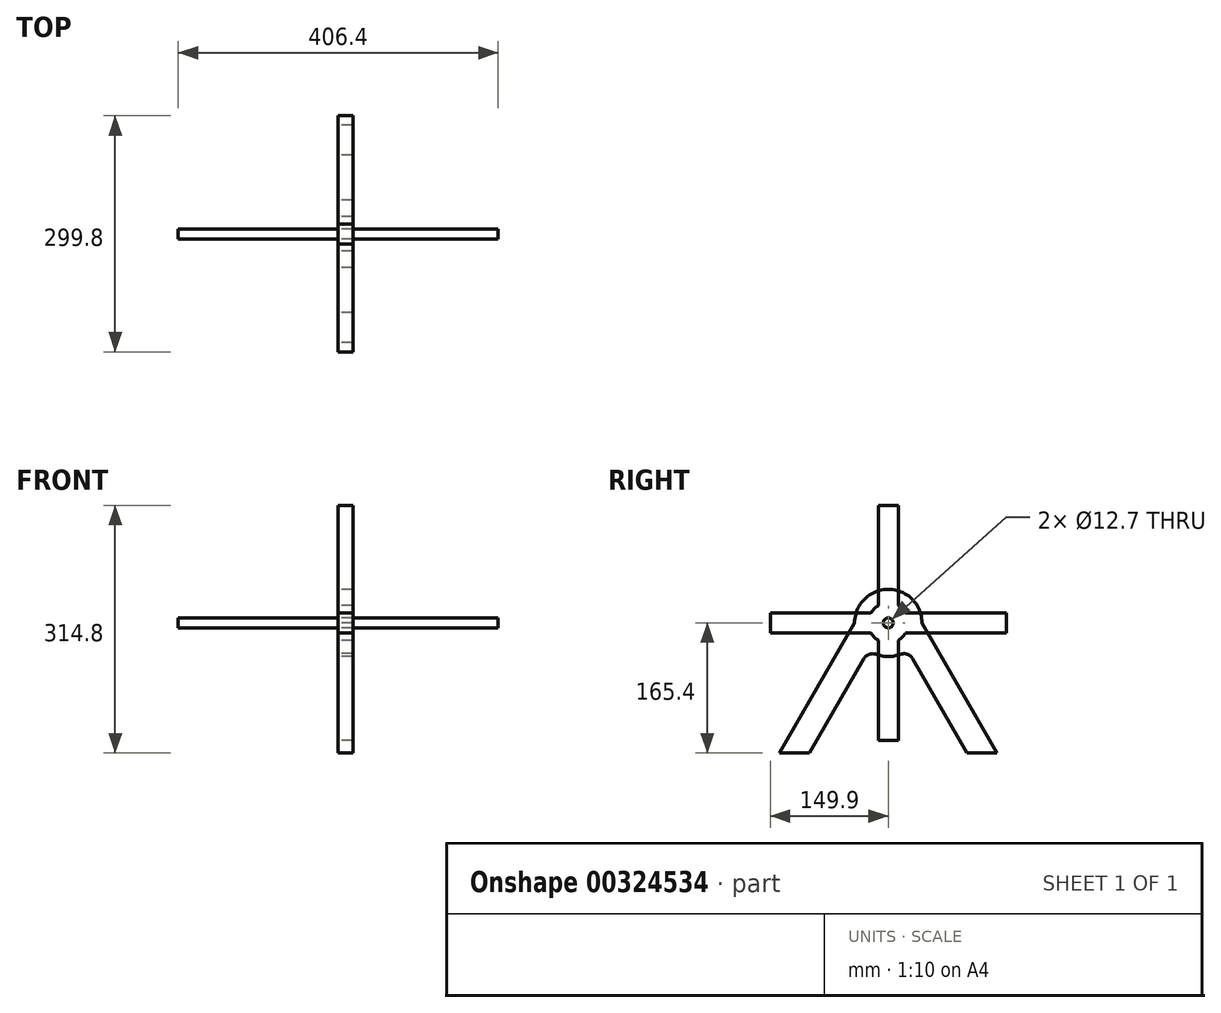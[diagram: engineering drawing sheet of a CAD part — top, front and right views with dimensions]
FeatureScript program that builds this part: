
annotation { "Feature Type Name" : "Feature", "Feature Type Description" : "" }
export const myFeature = defineFeature(function(context is Context, id is Id, definition is map)
    precondition{}
    {
        {
            var Q0;
            Q0=qCreatedBy(makeId("Right.planeOp"),FACE);
            var sketch = newSketch(context, id + "F0", { "sketchPlane" : qUnion([Q0])});
            skCircle(sketch, "E0", {"center": v(0, 0) * mm, "radius": 152.4 * mm});
            skSolve(sketch);
        }
        {
            var Q0;
            Q0=qCreatedBy(makeId("Right.planeOp"),FACE);
            var sketch = newSketch(context, id + "F1", { "sketchPlane" : qUnion([Q0])});
            skArc(sketch, "E1", {"start": v(-12.7, 22) * mm, "mid": v(-17.96, 17.96) * mm, "end": v(-22, 12.7) * mm});
            skCircle(sketch, "E2", {"center": v(0, 0) * mm, "radius": 6.35 * mm});
            skLineSegment(sketch, "E3.bottom", {"start": v(149.9, -12.7) * mm, "end": v(22, -12.7) * mm});
            skLineSegment(sketch, "E3.top", {"start": v(149.9, 12.7) * mm, "end": v(22, 12.7) * mm});
            skLineSegment(sketch, "E3.left", {"start": v(149.9, -12.7) * mm, "end": v(149.9, 12.7) * mm});
            skLineSegment(sketch, "E3.right", {"start": v(-149.9, -12.7) * mm, "end": v(-149.9, 12.7) * mm});
            skLineSegment(sketch, "E4.bottom", {"start": v(12.7, -149.4) * mm, "end": v(-12.7, -149.4) * mm});
            skLineSegment(sketch, "E4.top", {"start": v(12.7, 149.4) * mm, "end": v(-12.7, 149.4) * mm});
            skLineSegment(sketch, "E4.left", {"start": v(12.7, -149.4) * mm, "end": v(12.7, -22) * mm});
            skLineSegment(sketch, "E4.right", {"start": v(-12.7, -149.4) * mm, "end": v(-12.7, -12.7) * mm});
            skLineSegment(sketch, "E5.trimOffspring", {"start": v(-22, 12.7) * mm, "end": v(-149.9, 12.7) * mm});
            skLineSegment(sketch, "E6.trimOffspring", {"start": v(12.7, 22) * mm, "end": v(12.7, 149.4) * mm});
            skLineSegment(sketch, "E7.trimOffspring", {"start": v(-22, -12.7) * mm, "end": v(-149.9, -12.7) * mm});
            skLineSegment(sketch, "E8.trimOffspring", {"start": v(-12.7, 22) * mm, "end": v(-12.7, 149.4) * mm});
            skArc(sketch, "E9.trimOffspring", {"start": v(22, 12.7) * mm, "mid": v(17.96, 17.96) * mm, "end": v(12.7, 22) * mm});
            skArc(sketch, "E10.trimOffspring", {"start": v(12.7, -22) * mm, "mid": v(17.96, -17.96) * mm, "end": v(22, -12.7) * mm});
            skArc(sketch, "E11.trimOffspring", {"start": v(-22, -12.7) * mm, "mid": v(-17.96, -17.96) * mm, "end": v(-12.7, -22) * mm});
            skSolve(sketch);
        }
        {
            var Q0;
            Q0 = qSketchRegion(id + "F1", true);
            extrude(context, id + "F2", {"entities" : qUnion([Q0]), "depth" : 19.05 * mm});
        }
        {
            var Q0;
            Q0=makeQuery(id+"F0.imprint","IMPRINT",FACE,{"disambiguationData":[TD([[makeQuery(id+"F0.imprint","IMPRINT",EDGE,{"derivedFrom":sQuery(id+"F0.wireOp",EDGE,"E0")}),1.0]])]});
            var sketch = newSketch(context, id + "F3", { "sketchPlane" : qUnion([Q0])});
            skCircle(sketch, "E12.0", {"center": v(0, 0) * mm, "radius": 6.35 * mm});
            skSolve(sketch);
        }
        {
            var Q0;
            Q0 = qSketchRegion(id + "F3", true);
            extrude(context, id + "F4", {"entities" : qUnion([Q0]), "endBound" : BoundingType.SYMMETRIC, "depth" : 406.4 * mm});
        }
        {
            var Q0;
            Q0=qCreatedBy(makeId("Right.planeOp"),FACE);
            var sketch = newSketch(context, id + "F5", { "sketchPlane" : qUnion([Q0])});
            skArc(sketch, "E13", {"start": v(-15.29, -39.94) * mm, "mid": v(0.03, -42.76) * mm, "end": v(15.33, -39.92) * mm});
            skLineSegment(sketch, "E14", {"start": v(-42.62, 0) * mm, "end": v(-138.12, -165.4) * mm});
            skLineSegment(sketch, "E15", {"start": v(100.16, -165.4) * mm, "end": v(138.26, -165.4) * mm});
            skLineSegment(sketch, "E16", {"start": v(138.26, -165.4) * mm, "end": v(42.76, 0) * mm});
            skPoint(sketch, "E17.visualSharp", {"position": v(-74.62, -129.72) * mm});
            skPoint(sketch, "E18.visualSharp", {"position": v(74.76, -129.72) * mm});
            skLineSegment(sketch, "E19", {"start": v(-100.02, -165.3) * mm, "end": v(-138.12, -165.4) * mm});
            skLineSegment(sketch, "E20", {"start": v(-100.02, -165.3) * mm, "end": v(-30.82, -45.45) * mm});
            skLineSegment(sketch, "E21", {"start": v(100.16, -165.4) * mm, "end": v(30.89, -45.42) * mm});
            skArc(sketch, "E22.trimOffspring", {"start": v(42.76, 0) * mm, "mid": v(-0.12, 42.76) * mm, "end": v(-42.76, -0.24) * mm});
            skPoint(sketch, "E23.visualSharp", {"position": v(24.78, -34.85) * mm});
            skArc(sketch, "E23.filletArc", {"start": v(30.89, -45.42) * mm, "mid": v(24.13, -39.8) * mm, "end": v(15.33, -39.92) * mm});
            skPoint(sketch, "E24.visualSharp", {"position": v(-24.73, -34.89) * mm});
            skArc(sketch, "E24.filletArc", {"start": v(-15.29, -39.94) * mm, "mid": v(-24.07, -39.83) * mm, "end": v(-30.82, -45.45) * mm});
            skCircle(sketch, "E25.0", {"center": v(0, 0) * mm, "radius": 6.35 * mm});
            skSolve(sketch);
        }
        {
            var Q0;
            Q0 = qSketchRegion(id + "F5", true);
            extrude(context, id + "F6", {"entities" : qUnion([Q0]), "depth" : 19.05 * mm});
        }
    });
